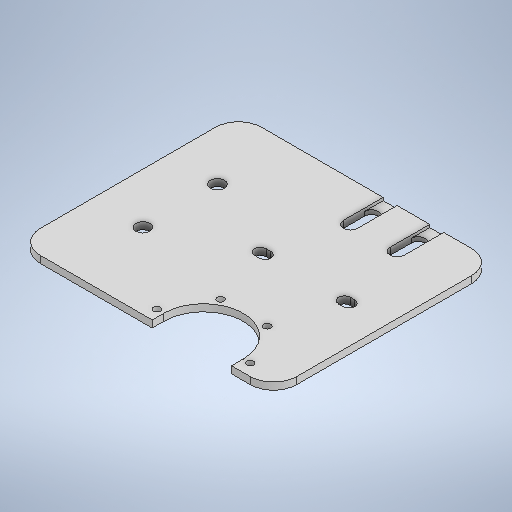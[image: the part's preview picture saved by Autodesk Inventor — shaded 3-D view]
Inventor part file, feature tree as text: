
AUTODESK INVENTOR PART (.ipt)
format: ipt  version: 2025.2 (Build 292293000, 293)  size: 332,800 bytes
history: native  units: mm
features: extrude x6, sketch x6, fillet x1
ambient origin geometry x8: Origin, YZ Plane, XZ Plane, XY Plane, X Axis, Y Axis, Z Axis, Center Point
bodies: Solid1 (feature_tree)
feature tree (13):
  extrude  "Extrusion1"  Depth=95.0mm
  sketch  "Sketch4"  dims[d15=20.0mm d16=6.0mm]
  extrude  "Extrusion3"  Depth=20.0mm
  extrude  "Extrusion5"  Depth=6.0mm
  extrude  "Extrusion6"  Depth=5.0mm
  extrude  "Extrusion7"  Depth=3.0mm
  extrude  "Extrusion8"  Depth=3.0mm
  fillet  "Fillet1"  Radius=3.0mm
  sketch  "Sketch1"  dims[d0=150.0mm d1=95.0mm]
  sketch  "Sketch6"  dims[d17=6.0mm d18=5.0mm]
  sketch  "Sketch7"  dims[d19=5.0mm d20=3.0mm]
  sketch  "Sketch8"  dims[d21=3.0mm d22=3.0mm d23=3.0mm d24=0.0mm d25=0.0mm d38=1.2mm d39=0.0mm d40=25.0mm d41=43.2mm d42=53.4mm d43=32.0mm d44=6.0mm d45=6.0mm d46=38.0mm d47=5.0mm d48=5.0mm d49=2.0mm d50=2.0mm d51=5.0mm d52=5.0mm d53=0.0mm d54=0.0mm d55=40.0mm d56=0.0mm d57=0.0mm d60=90.0mm d61=50.0mm d62=40.0mm d63=20.0mm d64=3.0mm d65=60.0mm d67=360.0deg d69=34.0mm d70=0.0mm d71=0.0mm d72=10.0mm d26=0.5mm d27=0.872665mm d28=0.5mm d29=0.872665mm]
  sketch  "Sketch Circular Pattern1"  dims[d2=3.0mm d3=0.0mm d14=20.0mm]
